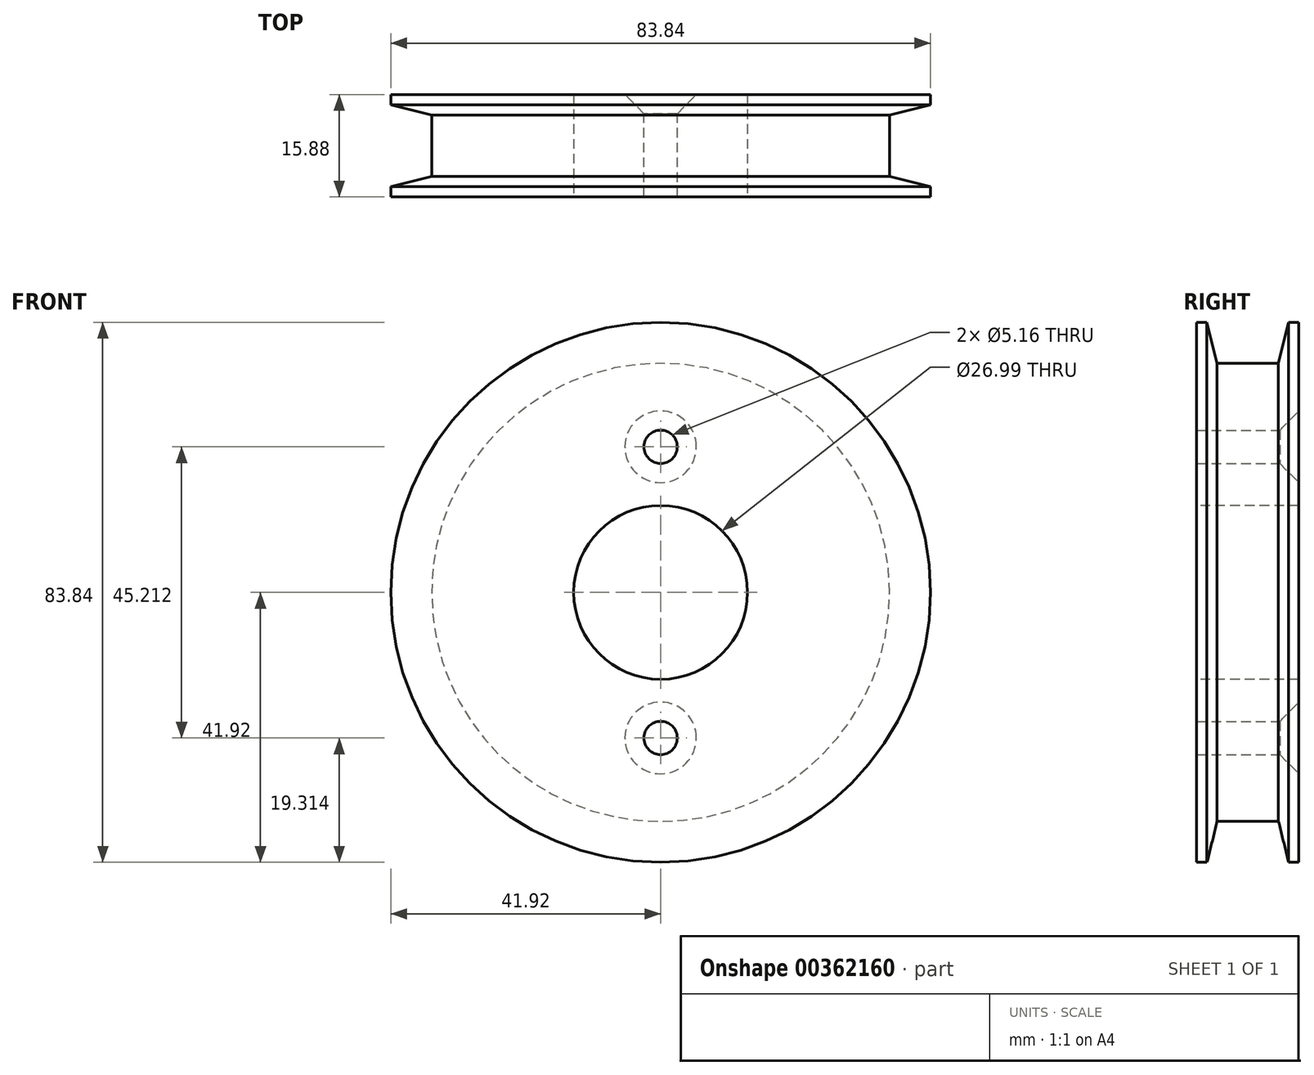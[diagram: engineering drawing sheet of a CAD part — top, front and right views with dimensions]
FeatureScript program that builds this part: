
annotation { "Feature Type Name" : "Feature", "Feature Type Description" : "" }
export const myFeature = defineFeature(function(context is Context, id is Id, definition is map)
    precondition{}
    {
        {
            var Q0;
            Q0=qCreatedBy(makeId("Right.planeOp"),FACE);
            var sketch = newSketch(context, id + "F0", { "sketchPlane" : qUnion([Q0])});
            skLineSegment(sketch, "E0", {"start": v(0, 13.5) * mm, "end": v(0, 41.92) * mm});
            skLineSegment(sketch, "E1", {"start": v(0, 41.92) * mm, "end": v(-3.17, 41.92) * mm});
            skLineSegment(sketch, "E2", {"start": v(-3.17, 41.92) * mm, "end": v(-3.17, 35.57) * mm});
            skLineSegment(sketch, "E3", {"start": v(-3.17, 35.57) * mm, "end": v(-12.7, 35.57) * mm});
            skLineSegment(sketch, "E4", {"start": v(-12.7, 35.57) * mm, "end": v(-12.7, 41.92) * mm});
            skLineSegment(sketch, "E5", {"start": v(-12.7, 41.92) * mm, "end": v(-15.87, 41.92) * mm});
            skLineSegment(sketch, "E6", {"start": v(-15.87, 41.92) * mm, "end": v(-15.87, 13.5) * mm});
            skLineSegment(sketch, "E7", {"start": v(-15.87, 0) * mm, "end": v(0, 0) * mm});
            skLineSegment(sketch, "E8", {"start": v(-15.87, 13.5) * mm, "end": v(0, 13.5) * mm});
            skSolve(sketch);
        }
        {
            var Q0;
            Q0=makeQuery(id+"F0.imprint","IMPRINT",FACE,{"disambiguationData":[TD([[makeQuery(id+"F0.imprint","IMPRINT",EDGE,{"derivedFrom":sQuery(id+"F0.wireOp",EDGE,"E0")}),1.0]])]});
            var Q1;
            Q1=sQuery(id+"F0.wireOp",EDGE,"E6");
            var Q2;
            Q2=sQuery(id+"F0.wireOp",EDGE,"E5");
            var Q3;
            Q3=sQuery(id+"F0.wireOp",EDGE,"E4");
            var Q4;
            Q4=sQuery(id+"F0.wireOp",EDGE,"E3");
            var Q5;
            Q5=sQuery(id+"F0.wireOp",EDGE,"E7");
            revolve(context, id + "F1", {"entities" : qUnion([Q0]), "surfaceEntities" : qUnion([Q1, Q2, Q3, Q4]), "axis" : qUnion([Q5]), "revolveType" : RevolveType.FULL});
        }
        {
            var Q0;
            Q0=makeQuery(id+"F1.opRevolve","SWEPT_EDGE",EDGE,{"disambiguationData":[OSD([sQuery(id+"F0.wireOp",EDGE,"E4"),sQuery(id+"F0.wireOp",EDGE,"E5")])]});
            chamfer(context, id + "F2", {"entities" : qUnion([Q0]), "chamferType" : ChamferType.TWO_OFFSETS, "width1" : 1.59 * mm, "oppositeDirection" : false, "width2" : 6.35 * mm, "tangentPropagation" : true});
        }
        {
            var Q0;
            Q0=makeQuery(id+"F1.opRevolve","SWEPT_EDGE",EDGE,{"disambiguationData":[OSD([sQuery(id+"F0.wireOp",EDGE,"E1"),sQuery(id+"F0.wireOp",EDGE,"E2")])]});
            chamfer(context, id + "F3", {"entities" : qUnion([Q0]), "chamferType" : ChamferType.TWO_OFFSETS, "width1" : 6.35 * mm, "oppositeDirection" : false, "width2" : 1.59 * mm, "tangentPropagation" : true});
        }
        {
            var Q0;
            Q0=makeQuery(id+"F1.opRevolve","SWEPT_FACE",FACE,{"disambiguationData":[OSD([sQuery(id+"F0.wireOp",EDGE,"E0")])]});
            var sketch = newSketch(context, id + "F4", { "sketchPlane" : qUnion([Q0])});
            skLineSegment(sketch, "E9", {"start": v(0, 0) * mm, "end": v(0, 22.6) * mm, "construction": true});
            skLineSegment(sketch, "E10", {"start": v(0, 0) * mm, "end": v(0, -22.6) * mm, "construction": true});
            skPoint(sketch, "E11", {"position": v(0, 22.6) * mm});
            skPoint(sketch, "E12", {"position": v(0, -22.6) * mm});
            skSolve(sketch);
        }
        {
            var Q0;
            Q0=sQuery(id+"F4.wireOp",VERTEX,"E11");
            var Q1;
            Q1=sQuery(id+"F4.wireOp",VERTEX,"E12");
            var Q2;
            Q2=makeQuery(id+"F1.opRevolve","SWEPT_BODY",BODY,{"disambiguationData":[OSD([sQuery(id+"F0.wireOp",EDGE,"E0"),sQuery(id+"F0.wireOp",EDGE,"E1"),sQuery(id+"F0.wireOp",EDGE,"E2"),sQuery(id+"F0.wireOp",EDGE,"E3"),sQuery(id+"F0.wireOp",EDGE,"E4"),sQuery(id+"F0.wireOp",EDGE,"E5"),sQuery(id+"F0.wireOp",EDGE,"E6"),sQuery(id+"F0.wireOp",EDGE,"E8")])]});
            hole(context, id + "F5", {"style" : HoleStyle.C_SINK, "endStyle" : HoleEndStyle.THROUGH, "holeDiameter" : 5.16 * mm, "cSinkDiameter" : 11.1 * mm, "cSinkAngle" : 90 * degree, "isTappedThrough" : true, "tappedDepth" : 12.7 * mm, "tapClearance" : 3, "startFromSketch" : true, "locations" : qUnion([Q0, Q1]), "scope" : qUnion([Q2])});
        }
    });
